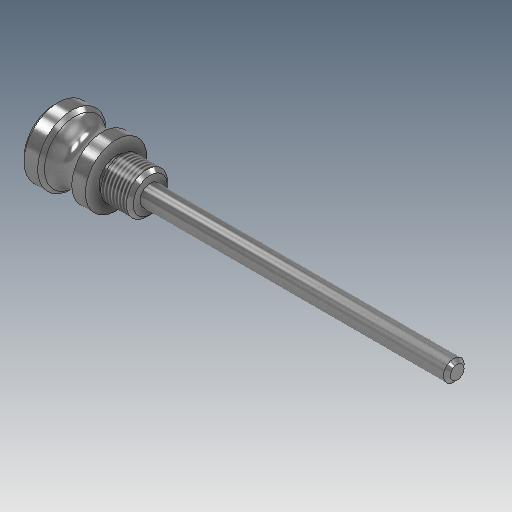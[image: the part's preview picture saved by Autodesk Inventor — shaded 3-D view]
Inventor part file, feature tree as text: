
AUTODESK INVENTOR PART (.ipt)
format: ipt  version: 2025 (Build 290162000, 162)  size: 180,736 bytes
history: native  units: in
note: dims shown in document units (in); Inventor stores cm internally (conversion verified against a paired STEP export)
features: revolve x1, thread x1, sketch x1
ambient origin geometry x8: Origin, YZ Plane, XZ Plane, XY Plane, X Axis, Y Axis, Z Axis, Center Point
bodies: 实体1 (feature_tree)
feature tree (3):
  revolve  "旋转1"  [1 undecoded]
  thread  "螺纹1"  [1 undecoded]
  sketch  "草图1"  dims[d1=0.1575in d2=0.4724in d3=0.2362in d0=0.3937in d4=45.0deg d5=0.0394in d6=45.0deg d7=0.0394in d8=0.2362in d9=0.2362in d10=45.0deg d11=0.0394in d12=0.1181in d13=0.1575in d14=0.3937in d16=1.1024in d17=0.3543in d18=0.0591in d19=0.0394in d20=90.0deg d21=45.0deg d22=0.0394in d23=3.937in d24=0.2953in d25=0.0in]
note: 2 required parameter values undecoded (feature->parameter linkage not recoverable at this tier; creation-order binding heuristic only, values carry confidence <= 0.55)